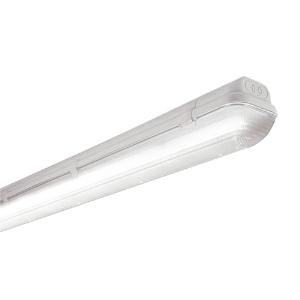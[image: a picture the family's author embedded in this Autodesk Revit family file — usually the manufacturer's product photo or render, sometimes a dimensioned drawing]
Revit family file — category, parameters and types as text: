
# Revit family: 3f_filippi_-_3f_linda_basic_3f_filippi_-_58762_-_3f_linda_led_basic_1x19w_l1270
name_source: partatom
category: Lighting Fixtures
units: mm (PartAtom-declared; Revit-internal decimal feet)

## family parameters
Cut with Voids When Loaded = No
Host = Face
Light Source = No
Part Type = Normal
Room Calculation Point = No
Round Connector Dimension = Use Diameter
Shared = No

## types (1)
- 3F Filippi - 3F Linda Basic (1 x LED, 2938 lm, 19 W, 4000 K)
    Apparent Load = 19 VA
    Approval mark = CE
    CIE Flux Codes = 44 77 94 97 100
    Color Rendering = 80
    Color Temperature = 4000 K
    Control Gear = Electronic ballast
    Default Elevation = 1800 mm
    Description = ILLUMINOTECHNICAL
Luminous efficiency 100% (DLOR 97%, ULOR 3%).
Initial luminous flux of the luminaire 2938 lm.
Controlled direct symmetric distribution.
Installation Interdistance Transv.D = 1.77 x hu - Long.D = 1.17 x hu.
Tabular UGR (CIE 117 - 4H-8H; S=0.25H; 70/50/20): RUG 20.8 - 21.8.
Beam angle: 109° - 64°.
Luminous efficacy 155 lm/W.
Lifetime (L92/B10): 30000 h. (tq+25°C)
Lifetime (L85/B10): 50000 h. (tq+25°C)
Lifetime (L75/B10): 80000 h. (tq+25°C)
Lifetime (L70/B10): 100000 h. (tq+25°C)
Lifetime (L75/B10): 50000 h. (tq+40°C)
Sudden decreased luminous flux after 50000 hours: 0% (C0).
Photobiological safety in compliance with IEC/TR 62778: RG0 risk exempt, (IEC 62471).
In compliance with IEC/EN 62722-2-1 - IEC/EN 62717 standards.

SOURCE
Linear LED module 19W/840.
Energy efficiency class (UE 2019/2020 - UE 2019/2015): D.
CIE 13.3 Colour rendering index: CRI >80 (R9 <50%).
IES TM-30 Fidelity Index: Rf = 84 Rg = 95.
CCT nominal colour temperature 4000 K.
Colour initial tolerance (MacAdam): SDCM 3.

MECHANICAL
Self-extinguishing V2 polycarbonate housing, injection moulded, RAL 7035 grey.
Ecologic anti-aging injected sealing gasket.
Diffuser in self-extinguishing V2 polycarbonate, photo-engraved interior, UV stabilised, injection moulded with smooth outer surface, tamper-proof opening.
Gear-holder reflector in hot-dip galvanised steel, painted with white polyester base.
Snug fit snap-lock clips for diffuser mounting, in polycarbonate.
Fixing brackets in stainless steel.
Possibility for technicians to access the interior of the luminaire.
Luminaire with limited surface temperature. - D - (EN 60598-2-24)
Dimensions: 1270x100 mm, height 100 mm. Weight 2.08 kg.
IP66 protection degree.
Mechanical strength to impacts IK10 (20 joule).
Glow-wire test resistance 850°C.

ELECTRICAL
Halogen Free electronic wiring 230V-50/60Hz, power factor 0.90, THD <25%, constant output current, SELV, class I, 1 driver.
Power of the luminaire 19 W.
ENEC - CE.
SAFE FLICKER: PstLM=<1 and SVM=<0.4 (IEC TR 61547-1 and IEC TR 63158), to ensure a more comfortable and safe light.
Luminaire compliant with EN 60598-2-22 for power supply from a centralised emergency system CPSS (Central Power Supply System), not incorporated in the luminaire - high risk areas excluded. The default power and flux are 100% in AC and 100% in DC.
Ambient temperature from -20°C to +40°C.
Temperature class T6 max 85°C.
Relative humidity UR: <85%.

INSTALLATION
Ceiling / Suspended / Wall.
All accessories dedicated to this product are available on the Catalog and on our website www.3F-Filippi.com.

APPLICATIONS
Suitable product for food production plants (HACCP), IFS (Food Version 6), BRC (GSFS Food Version 7).
Dry, dusty indoor environments, subject to occasional water splashes.
Virtually shatterproof polycarbonate compatibly with the fumes / atmospheres that compromise the elasticity of plastic materials.
Not suitable for installation on surfaces subject to important vibrations, exposed to weather conditions, on ropes or poles.
Suitable for illumination of public car parks and parking grounds referred to DIN 67528:2018-04.

WARNING
Fixture not suitable for cold stores with an ambient temperature <0°C and/or relative humidity >85%.
Luminaire designed for disposal/recycling at end-of-life.
Replaceable (LED only) light source by a professional. Replaceable control gear by a professional.
    Height = 100 mm  [stored 0.328084 ft]
    Lamp = 1 x LED
    Lamp Light Flux = 2938 lm
    Lamp Power = 19 W
    Lamp count = 1
    Length = 1270 mm
    Lifetime = 50000 h
    Luminous efficacy = 155 lm/W
    Manufacturer = 3F Filippi
    ModVariant = No
    Model = 3F Filippi - 58762 - 3F Linda LED Basic 1x19W L1270
    Mounting Place = Ceiling
    Mounting Type = Pendant
    Number of Poles = 1
    OnlyDefault = Yes
    Power Factor = 1
    Product Name = 3F Filippi - 3F Linda Basic
    Product group = pendant luminaire
    ProductGroupID = 9
    Protection Class = Protection class I
    Protection Degree = IP 66
    RLX_Detail_Level = 1
    RLX_Emergency_Light_Flux = 0 lm
    RLX_Emergency_Type = 0
    RLX_Emergency_Type_DB = No
    RlxData = <blob elided: 59441 chars, md5=988f1a04>
    Socket = socket
    Standby Power = 0 W
    System Light Flux = 2938 lm
    System Power = 19 W
    Type Comments = Product without accessories
    Type Image = 3ffilippi_3f_linda_led_basic_1x.jpg
    URL = http://relux.com
    VarID = ---
    Voltage = 0 V
    Weight = 0.00 kg
    Width = 100 mm  [stored 0.328084 ft]

note: [stored X ft] marks values corroborated as IEEE doubles in the binary element streams (Revit-internal decimal feet)

## geometry (parser evidence)
native form markers: Blend x4, Sweep x10
no freeform markers — native parametric forms only
